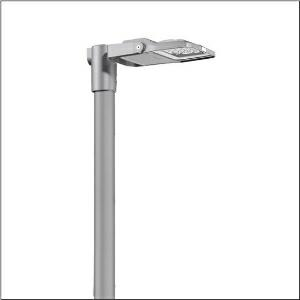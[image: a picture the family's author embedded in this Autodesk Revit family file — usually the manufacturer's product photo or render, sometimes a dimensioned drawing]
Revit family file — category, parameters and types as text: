
# Revit family: floodlight_fl_21_iq_micro___pl52_5xa7762a2d3a_f78f
name_source: partatom
category: Lighting Fixtures
units: mm (PartAtom-declared; Revit-internal decimal feet)

## family parameters
Cut with Voids When Loaded = No
Host = Face
Light Source = No
Part Type = Normal
Room Calculation Point = No
Round Connector Dimension = Use Diameter
Shared = No

## types (1)
- --- (1 x LED, 2890 lm, 23.1 W, 3000K)
    Apparent Load = 23 VA
    CIE Flux Codes = 26 60 98 100 100
    Color Rendering = 70
    Color Temperature = 3000K
    Default Elevation = 1800 mm
    Description = Floodlight FL 21 iQ micro, floodlight, primary light control with lens, of PMMA, primary optical cover: protective disc, of toughened safety glass, transparent, light distribution: PL52, light emission: direct distribution, installation type: surface-mounted, lamps: LED, High Power LED, rated values: 2.890lm | 23,1W | 125,1lm/W (begin service life); end service life: 2.890lm | 23,8W; at 50% lumin. flux: 1.445lm | 11W | 131,4lm/W, colour temperature: 3000K, colour rendering: CRI > 70, light colour: 730, light setting 1 begin service life: 100% | 2.890lm | 23,1W | 125,1lm/W | 3.000K, light setting 1 end service life: 23,8W, further light settings possible, control: Auto-Match, Temp-Guard, Night-Set, Smart-Wire, Desk-Remote (wireless, voltage-free reading and setting of iQ features in the workshop via application-optimized NFC function/RFID function), optimised constant luminous flux control (CLO 2.0), Street-Remote, pre-setting: linear dimming characteristic, with terminal, 6-pole, mains connection: 220..240V, AC, 50/60Hz, luminaire housing, of diecast aluminium, powder-coated, SITECO metallic grey (DB 702S), corrosivity category C5 mid according to DIN EN ISO 12944suitable for swimming poolschlorine-resistant, sealing non-destructively replaceable, please order mast flange separately, mast bracket, of steel, galvanised, powder-coated, SITECO metallic grey (DB 702S), protection rating (complete): IP66, insulation class (complete): insulation class II (safety insulation), certification: CE, ENEC, VDE, protection symbol: D, impact resistance: IK07, permissible operating ambient temperature: -40..+40°C, permissible operating ambient temperature for outdoor applications: -40..+50°C, standard: DIN EN 12944, LABS conformity tested according to VDMA 24364:2018-05, packaging unit: 1 piece

Light Distribution: PL52
    Height = 65 mm
    Lamp = 1 x LED
    Lamp Light Flux = 2890 lm
    Lamp Power = 23.1 W
    Lamp count = 1
    Length = 312 mm
    Luminous efficacy = 125 lm/W
    Manufacturer = Siteco
    ModVariant = No
    Model = 5XA7762A2D3A
    Number of Poles = 1
    OnlyDefault = Yes
    Power Factor = 1
    Product Name = Floodlight FL 21 iQ micro | PL52
    Product group = floodlight | pylon annexe
    ProductGroupID = 6201
    Protection Class = Protection class II
    Protection Degree = IP 66
    RLX_Detail_Level = 1
    RLX_Emergency_Light_Flux = 0 lm
    RLX_Emergency_Type = 0
    RLX_Emergency_Type_DB = No
    RlxData = <blob elided: 102153 chars, md5=3d268ef9>
    Socket = socket
    Standby Power = 0 W
    System Light Flux = 2890 lm
    System Power = 23 W
    Type Comments = factory setting: luminous flux: 100 % | dim-lin: 254 | 455 mA
    Type Image = l_1007121.jpg
    URL = http://relux.com
    VarID = @adj_177327
    Voltage = 0 V
    Weight = 0.00 kg
    Width = 230 mm

## geometry (parser evidence)
native form markers: Blend x4, Sweep x10
no freeform markers — native parametric forms only
